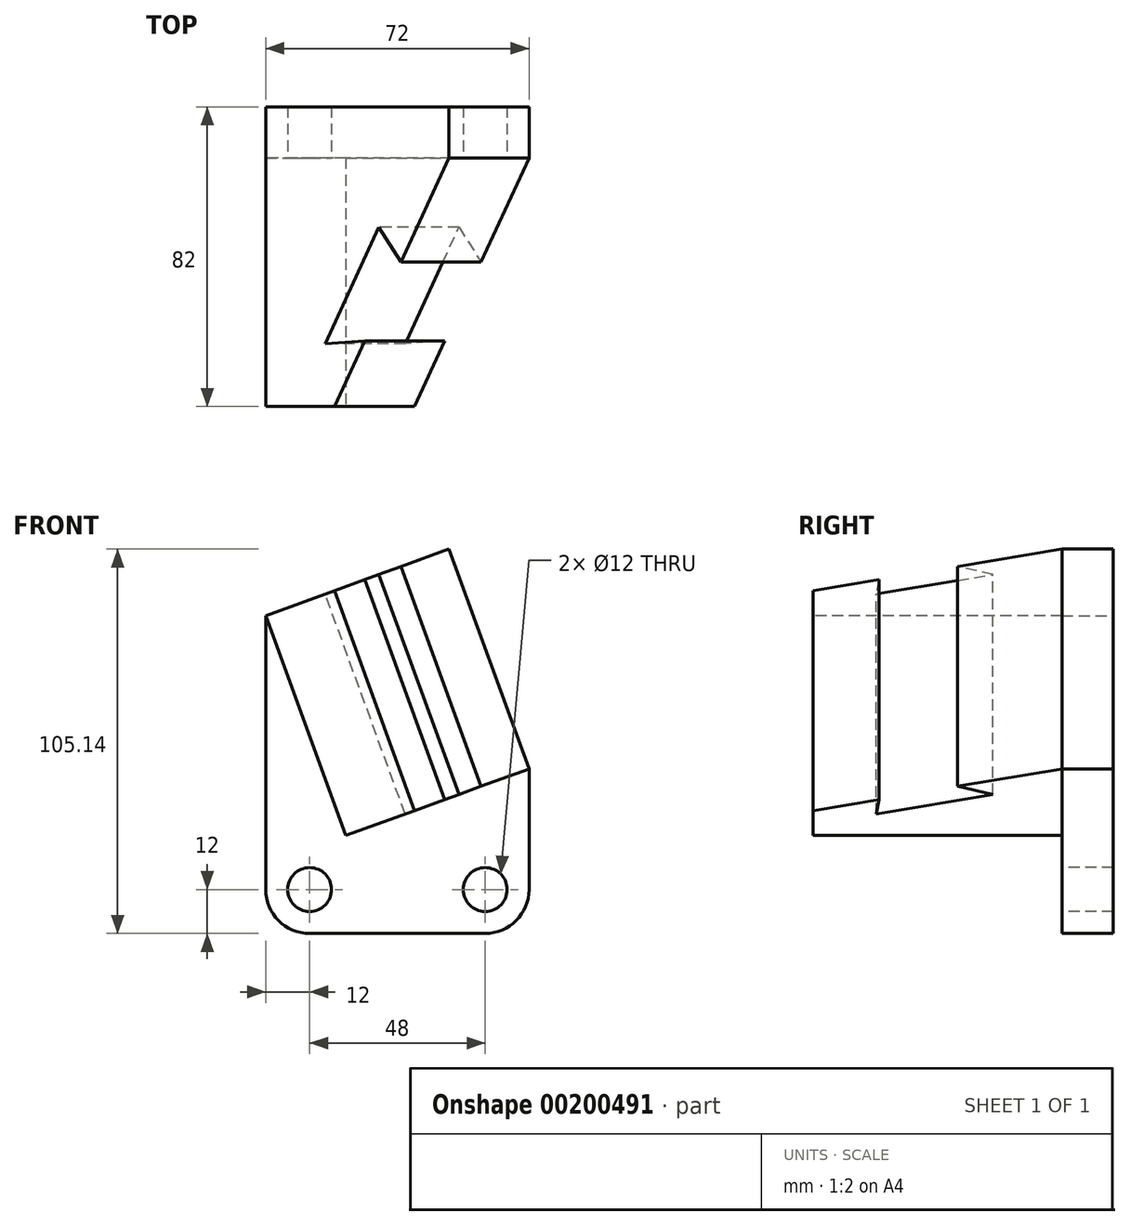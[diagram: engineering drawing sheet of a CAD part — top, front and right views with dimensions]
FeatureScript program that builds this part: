
annotation { "Feature Type Name" : "Feature", "Feature Type Description" : "" }
export const myFeature = defineFeature(function(context is Context, id is Id, definition is map)
    precondition{}
    {
        {
            var Q0;
            Q0=qCreatedBy(makeId("Front.planeOp"),FACE);
            var sketch = newSketch(context, id + "F0", { "sketchPlane" : qUnion([Q0])});
            skLineSegment(sketch, "E0", {"start": v(0, 0) * mm, "end": v(0, 86.9) * mm});
            skLineSegment(sketch, "E1", {"start": v(0, 86.9) * mm, "end": v(50.11, 105.14) * mm});
            skLineSegment(sketch, "E2", {"start": v(50.11, 105.14) * mm, "end": v(72, 45) * mm});
            skLineSegment(sketch, "E3", {"start": v(72, 45) * mm, "end": v(72, 0) * mm});
            skLineSegment(sketch, "E4", {"start": v(72, 0) * mm, "end": v(0, 0) * mm});
            skLineSegment(sketch, "E5", {"start": v(0, 86.9) * mm, "end": v(21.89, 26.76) * mm, "construction": true});
            skLineSegment(sketch, "E6", {"start": v(21.89, 26.76) * mm, "end": v(72, 45) * mm, "construction": true});
            skSolve(sketch);
        }
        {
            var Q0;
            Q0=makeQuery(id+"F0.imprint","IMPRINT",FACE,{"disambiguationData":[TD([[makeQuery(id+"F0.imprint","IMPRINT",EDGE,{"derivedFrom":sQuery(id+"F0.wireOp",EDGE,"E0")}),-1.0]])]});
            extrude(context, id + "F1", {"entities" : qUnion([Q0]), "depth" : 14 * mm});
        }
        {
            var Q0;
            Q0=makeQuery(id+"F1.opExtrude","SWEPT_FACE",FACE,{"disambiguationData":[OSD([sQuery(id+"F0.wireOp",EDGE,"E1")])]});
            var sketch = newSketch(context, id + "F2", { "sketchPlane" : qUnion([Q0])});
            skLineSegment(sketch, "E7", {"start": v(29.72, -14) * mm, "end": v(29.72, -82) * mm});
            skLineSegment(sketch, "E8", {"start": v(29.72, -82) * mm, "end": v(49.72, -82) * mm});
            skLineSegment(sketch, "E9", {"start": v(49.72, -82) * mm, "end": v(58.52, -64.04) * mm});
            skLineSegment(sketch, "E10", {"start": v(83.05, -14) * mm, "end": v(29.72, -14) * mm});
            skLineSegment(sketch, "E11", {"start": v(58.52, -64.04) * mm, "end": v(47, -64.82) * mm});
            skLineSegment(sketch, "E12", {"start": v(47, -64.82) * mm, "end": v(62.65, -32.9) * mm});
            skLineSegment(sketch, "E13", {"start": v(62.65, -32.9) * mm, "end": v(69.09, -42.49) * mm});
            skLineSegment(sketch, "E14.trimOffspring", {"start": v(69.09, -42.49) * mm, "end": v(83.05, -14) * mm});
            skSolve(sketch);
        }
        {
            var Q0;
            Q0=makeQuery(id+"F2.imprint","IMPRINT",FACE,{"disambiguationData":[TD([[makeQuery(id+"F2.imprint","IMPRINT",EDGE,{"derivedFrom":sQuery(id+"F2.wireOp",EDGE,"E7")}),1.0]])]});
            var Q1;
            Q1=makeQuery(id+"F1.opExtrude","CAP_VERTEX",VERTEX,{"disambiguationData":[OSD([sQuery(id+"F0.wireOp",EDGE,"E2"),sQuery(id+"F0.wireOp",EDGE,"E3")])],"isStart":false});
            extrude(context, id + "F3", {"entities" : qUnion([Q0]), "operationType" : NewBodyOperationType.ADD, "endBound" : BoundingType.UP_TO_VERTEX, "oppositeDirection" : true, "endBoundEntityVertex" : qUnion([Q1]), "depth" : 25 * mm});
        }
        {
            var Q0;
            Q0=makeQuery(id+"F1.opExtrude","SWEPT_EDGE",EDGE,{"disambiguationData":[OSD([sQuery(id+"F0.wireOp",EDGE,"E0"),sQuery(id+"F0.wireOp",EDGE,"E4")])]});
            var Q1;
            Q1=makeQuery(id+"F1.opExtrude","SWEPT_EDGE",EDGE,{"disambiguationData":[OSD([sQuery(id+"F0.wireOp",EDGE,"E3"),sQuery(id+"F0.wireOp",EDGE,"E4")])]});
            fillet(context, id + "F4", {"entities" : qUnion([Q0, Q1]), "radius" : 12 * mm, "tangentPropagation" : true, "allowEdgeOverflow" : false});
        }
        {
            var Q0;
            Q0=makeQuery(id+"F1.opExtrude","CAP_FACE",FACE,{"disambiguationData":[OSD([sQuery(id+"F0.wireOp",EDGE,"E0"),sQuery(id+"F0.wireOp",EDGE,"E1"),sQuery(id+"F0.wireOp",EDGE,"E2"),sQuery(id+"F0.wireOp",EDGE,"E3"),sQuery(id+"F0.wireOp",EDGE,"E4")])],"isStart":false});
            var sketch = newSketch(context, id + "F5", { "sketchPlane" : qUnion([Q0])});
            skCircle(sketch, "E15", {"center": v(12, 12) * mm, "radius": 6 * mm});
            skCircle(sketch, "E16", {"center": v(60, 12) * mm, "radius": 6 * mm});
            skSolve(sketch);
        }
        {
            var Q0;
            Q0=makeQuery(id+"F5.imprint","IMPRINT",FACE,{"disambiguationData":[TD([[makeQuery(id+"F5.imprint","IMPRINT",EDGE,{"derivedFrom":sQuery(id+"F5.wireOp",EDGE,"E15")}),1.0]])]});
            var Q1;
            Q1=makeQuery(id+"F5.imprint","IMPRINT",FACE,{"disambiguationData":[TD([[makeQuery(id+"F5.imprint","IMPRINT",EDGE,{"derivedFrom":sQuery(id+"F5.wireOp",EDGE,"E16")}),1.0]])]});
            extrude(context, id + "F6", {"entities" : qUnion([Q0, Q1]), "operationType" : NewBodyOperationType.REMOVE, "endBound" : BoundingType.UP_TO_NEXT, "oppositeDirection" : true, "depth" : 25 * mm});
        }
    });
